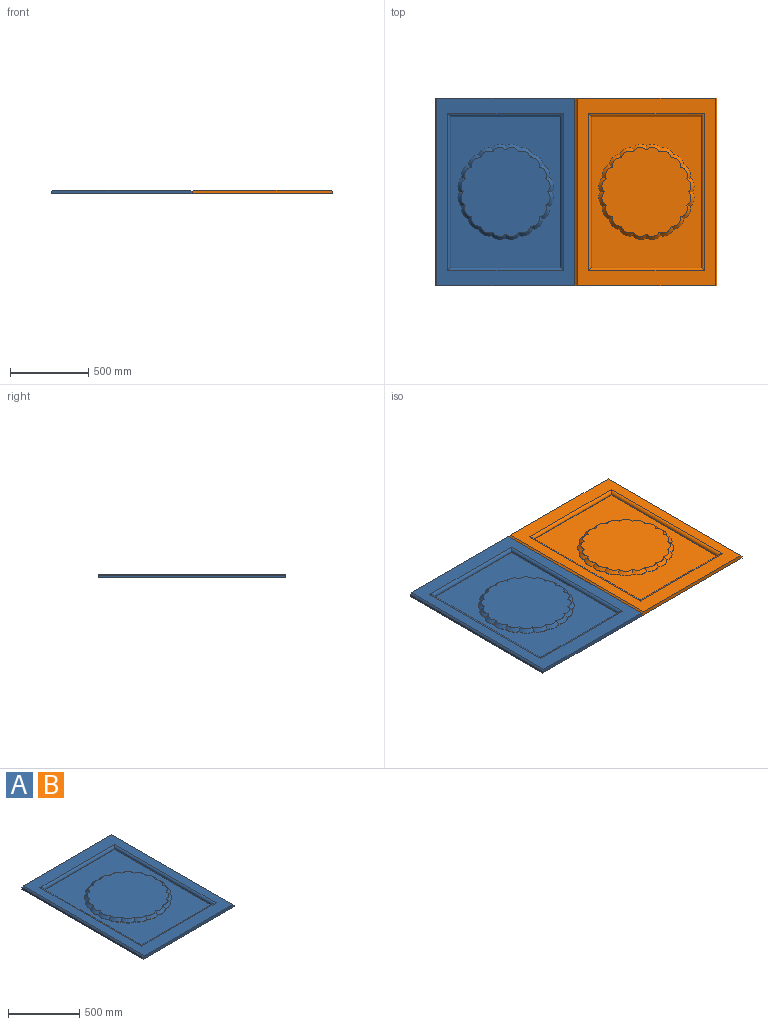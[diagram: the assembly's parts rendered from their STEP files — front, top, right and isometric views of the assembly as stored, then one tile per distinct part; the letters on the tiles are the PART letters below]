
ASSEMBLY  parts=2 mates=1
PART A: 58 faces, bbox 900x1200x25 mm
  f0: plane 1200x880mm, normal (0,0,1), area 312634.2mm2, adj f1,f3,f52,f53,f54,f55,f56,f57
  f1: plane 900x25mm, normal (0,1,0), area 22400mm2, adj f0,f2,f4,f5,f56,f57
  f2: plane 1200x15mm, normal (-1,0,0), area 18000mm2, adj f1,f3,f5,f56
  f3: plane 900x25mm, normal (0,-1,0), area 22400mm2, adj f0,f2,f4,f5,f56,f57
  f4: plane 1200x15mm, normal (1,0,0), area 18000mm2, adj f1,f3,f5,f57
  f5: plane 1200x900mm, normal (0,0,-1), area 1080000mm2, adj f1,f2,f3,f4
  f6: plane 700.7x2mm, normal (0,-1,0), area 1401.4mm2, adj f7,f29,f30,f52
  f7: plane 963.6x2mm, normal (1,0,0), area 1927.2mm2, adj f6,f8,f30,f53
  f8: plane 700.7x2mm, normal (0,1,0), area 1401.4mm2, adj f7,f29,f30,f55
  f9: cylinder r=73.18mm len=90.98mm, axis (0,0,1), area 199.3mm2, adj f10,f28,f30,f44
  f10: cylinder r=73.18mm len=82.07mm, axis (0,0,1), area 199.3mm2, adj f9,f11,f30,f46
  f11: cylinder r=73.18mm len=65.13mm, axis (0,0,1), area 199.3mm2, adj f10,f12,f30,f48
  f12: cylinder r=73.18mm len=82.07mm, axis (0,0,1), area 199.3mm2, adj f11,f13,f30,f50
  f13: cylinder r=73.18mm len=90.98mm, axis (0,0,1), area 199.3mm2, adj f12,f14,f30,f51
  f14: cylinder r=73.18mm len=90.98mm, axis (0,0,1), area 199.3mm2, adj f13,f15,f30,f49
  f15: cylinder r=73.18mm len=82.07mm, axis (0,0,1), area 199.3mm2, adj f14,f16,f30,f47
  f16: cylinder r=73.18mm len=65.13mm, axis (0,0,1), area 199.3mm2, adj f15,f17,f30,f45
  f17: cylinder r=73.18mm len=82.07mm, axis (0,0,1), area 199.3mm2, adj f16,f18,f30,f43
  f18: cylinder r=73.18mm len=90.98mm, axis (0,0,1), area 199.3mm2, adj f17,f19,f30,f41
  f19: cylinder r=73.18mm len=90.98mm, axis (0,0,1), area 199.3mm2, adj f18,f20,f30,f39
  f20: cylinder r=73.18mm len=82.07mm, axis (0,0,1), area 199.3mm2, adj f19,f21,f30,f37
  f21: cylinder r=73.18mm len=65.13mm, axis (0,0,1), area 199.3mm2, adj f20,f22,f30,f35
  f22: cylinder r=73.18mm len=82.07mm, axis (0,0,1), area 199.3mm2, adj f21,f23,f30,f33
  f23: cylinder r=73.18mm len=90.98mm, axis (0,0,1), area 199.3mm2, adj f22,f24,f30,f32
  f24: cylinder r=73.18mm len=90.98mm, axis (0,0,1), area 199.3mm2, adj f23,f25,f30,f34
  f25: cylinder r=73.18mm len=82.07mm, axis (0,0,1), area 199.3mm2, adj f24,f26,f30,f36
  f26: cylinder r=73.18mm len=65.13mm, axis (0,0,1), area 199.3mm2, adj f25,f27,f30,f38
  f27: cylinder r=73.18mm len=82.07mm, axis (0,0,1), area 199.3mm2, adj f26,f28,f30,f40
  f28: cylinder r=73.18mm len=90.98mm, axis (0,0,1), area 199.3mm2, adj f9,f27,f30,f42
  f29: plane 963.6x2mm, normal (-1,0,0), area 1927.2mm2, adj f6,f8,f30,f54
  f30: plane 963.6x700.7mm, normal (0,0,1), area 386833.9mm2, adj f6,f7,f8,f9,f10,f11,f12,f13
  f31: plane 568.42x568.42mm, normal (0,0,1), area 249120mm2, adj f32,f33,f34,f35,f36,f37,f38,f39
  f32: cone r=53.18mm half-angle=45deg, axis (0,0,-1), area 2774.7mm2, adj f23,f31,f33,f34
  f33: cone r=53.18mm half-angle=45deg, axis (0,0,-1), area 2774.7mm2, adj f22,f31,f32,f35
  f34: cone r=53.18mm half-angle=45deg, axis (0,0,-1), area 2774.7mm2, adj f24,f31,f32,f36
  f35: cone r=53.18mm half-angle=45deg, axis (0,0,-1), area 2774.7mm2, adj f21,f31,f33,f37
  f36: cone r=53.18mm half-angle=45deg, axis (0,0,-1), area 2774.7mm2, adj f25,f31,f34,f38
  f37: cone r=53.18mm half-angle=45deg, axis (0,0,-1), area 2774.7mm2, adj f20,f31,f35,f39
  f38: cone r=53.18mm half-angle=45deg, axis (0,0,-1), area 2774.7mm2, adj f26,f31,f36,f40
  f39: cone r=53.18mm half-angle=45deg, axis (0,0,-1), area 2774.7mm2, adj f19,f31,f37,f41
  f40: cone r=53.18mm half-angle=45deg, axis (0,0,-1), area 2774.7mm2, adj f27,f31,f38,f42
  f41: cone r=53.18mm half-angle=45deg, axis (0,0,-1), area 2774.7mm2, adj f18,f31,f39,f43
  f42: cone r=53.18mm half-angle=45deg, axis (0,0,-1), area 2774.7mm2, adj f28,f31,f40,f44
  f43: cone r=53.18mm half-angle=45deg, axis (0,0,-1), area 2774.7mm2, adj f17,f31,f41,f45
  f44: cone r=53.18mm half-angle=45deg, axis (0,0,-1), area 2774.7mm2, adj f9,f31,f42,f46
  f45: cone r=53.18mm half-angle=45deg, axis (0,0,-1), area 2774.7mm2, adj f16,f31,f43,f47
  f46: cone r=53.18mm half-angle=45deg, axis (0,0,-1), area 2774.7mm2, adj f10,f31,f44,f48
  f47: cone r=53.18mm half-angle=45deg, axis (0,0,-1), area 2774.7mm2, adj f15,f31,f45,f49
  f48: cone r=53.18mm half-angle=45deg, axis (0,0,-1), area 2774.7mm2, adj f11,f31,f46,f50
  f49: cone r=53.18mm half-angle=45deg, axis (0,0,-1), area 2774.7mm2, adj f14,f31,f47,f51
  f50: cone r=53.18mm half-angle=45deg, axis (0,0,-1), area 2774.7mm2, adj f12,f31,f48,f51
  f51: cone r=53.18mm half-angle=45deg, axis (0,0,-1), area 2774.7mm2, adj f13,f31,f49,f50
  f52: cylinder r=20mm len=740.7mm, axis (1,0,0), area 22469.8mm2, adj f0,f6,f53,f54
  f53: cylinder r=20mm len=1003.6mm, axis (0,1,0), area 30729mm2, adj f0,f7,f52,f55
  f54: cylinder r=20mm len=1003.6mm, axis (0,-1,0), area 30729mm2, adj f0,f29,f52,f55
  f55: cylinder r=20mm len=740.7mm, axis (-1,0,0), area 22469.8mm2, adj f0,f8,f53,f54
  f56: plane 1200x10mm, normal (-0.71,0,0.71), area 16970.6mm2, adj f0,f1,f2,f3
  f57: plane 1200x10mm, normal (0.71,0,0.71), area 16970.6mm2, adj f0,f1,f3,f4
PART B: same geometry as A
PLACE A t=(36.69,-293.48,127.23)mm fixed
PLACE B t=(936.69,-293.48,127.23)mm
MATE fastened A.f4 <-> B.f2  axis (1,0,0) through (-153.09,-255.02,134.73)mm
